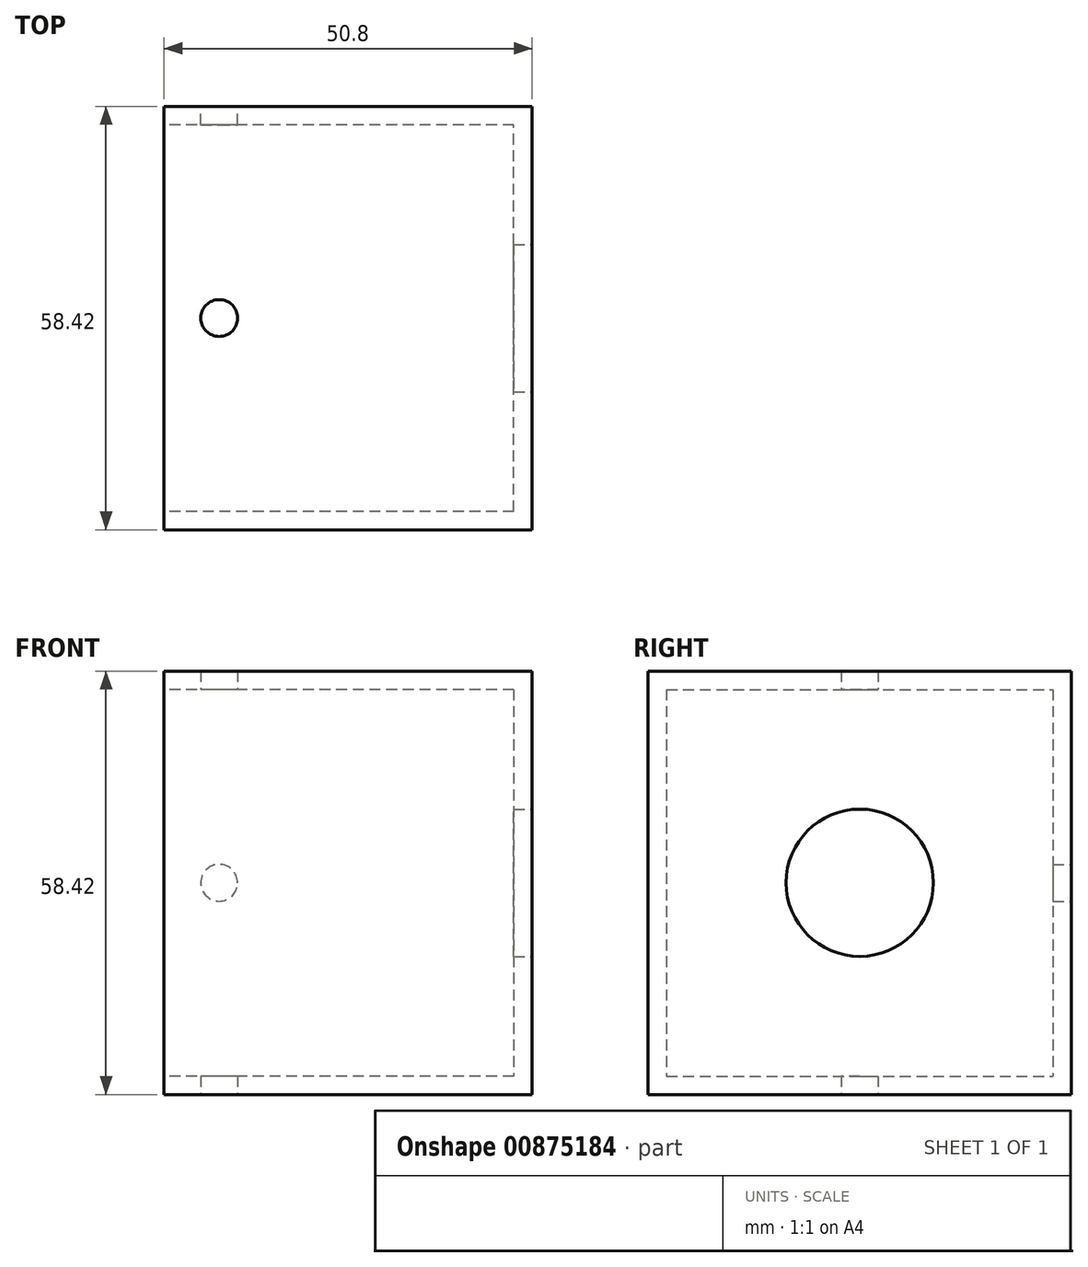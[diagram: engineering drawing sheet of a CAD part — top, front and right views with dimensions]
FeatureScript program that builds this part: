
annotation { "Feature Type Name" : "Feature", "Feature Type Description" : "" }
export const myFeature = defineFeature(function(context is Context, id is Id, definition is map)
    precondition{}
    {
        {
            var Q0;
            Q0=qCreatedBy(makeId("Right.planeOp"),FACE);
            var sketch = newSketch(context, id + "F0", { "sketchPlane" : qUnion([Q0])});
            skLineSegment(sketch, "E0.bottom", {"start": v(-29.2, 29.21) * mm, "end": v(29.21, 29.21) * mm});
            skLineSegment(sketch, "E0.top", {"start": v(-29.21, -29.2) * mm, "end": v(29.2, -29.2) * mm});
            skLineSegment(sketch, "E0.left", {"start": v(-29.2, 29.21) * mm, "end": v(-29.21, -29.2) * mm});
            skLineSegment(sketch, "E0.right", {"start": v(29.21, 29.21) * mm, "end": v(29.2, -29.2) * mm});
            skPoint(sketch, "E0.middle", {"position": v(0, 0) * mm});
            skSolve(sketch);
        }
        {
            var Q0;
            Q0=makeQuery(id+"F0.imprint","IMPRINT",FACE,{"disambiguationData":[TD([[makeQuery(id+"F0.imprint","IMPRINT",EDGE,{"derivedFrom":sQuery(id+"F0.wireOp",EDGE,"E0.bottom")}),-1.0]])]});
            extrude(context, id + "F1", {"entities" : qUnion([Q0]), "depth" : 50.8 * mm, "offsetDistance" : 25.4 * mm});
        }
        {
            var Q0;
            Q0=makeQuery(id+"F1.opExtrude","CAP_FACE",FACE,{"disambiguationData":[OSD([sQuery(id+"F0.wireOp",EDGE,"E0.bottom"),sQuery(id+"F0.wireOp",EDGE,"E0.top"),sQuery(id+"F0.wireOp",EDGE,"E0.left"),sQuery(id+"F0.wireOp",EDGE,"E0.right")])],"isStart":true});
            shell(context, id + "F2", {"entities" : qUnion([Q0]), "thickness" : 2.54 * mm});
        }
        {
            var Q0;
            Q0=makeQuery(id+"F1.opExtrude","CAP_FACE",FACE,{"disambiguationData":[OSD([sQuery(id+"F0.wireOp",EDGE,"E0.bottom"),sQuery(id+"F0.wireOp",EDGE,"E0.top"),sQuery(id+"F0.wireOp",EDGE,"E0.left"),sQuery(id+"F0.wireOp",EDGE,"E0.right")])],"isStart":false});
            var sketch = newSketch(context, id + "F3", { "sketchPlane" : qUnion([Q0])});
            skCircle(sketch, "E1", {"center": v(0, 0) * mm, "radius": 10.16 * mm});
            skSolve(sketch);
        }
        {
            var Q0;
            Q0=makeQuery(id+"F3.imprint","IMPRINT",FACE,{"disambiguationData":[TD([[makeQuery(id+"F3.imprint","IMPRINT",EDGE,{"derivedFrom":sQuery(id+"F3.wireOp",EDGE,"E1")}),1.0]])]});
            var Q1;
            Q1=sQuery(id+"F3.wireOp",EDGE,"E1");
            extrude(context, id + "F4", {"entities" : qUnion([Q0]), "operationType" : NewBodyOperationType.REMOVE, "surfaceEntities" : qUnion([Q1]), "oppositeDirection" : true, "depth" : 25.4 * mm, "offsetDistance" : 25.4 * mm});
        }
        {
            var Q0;
            Q0=makeQuery(id+"F1.opExtrude","SWEPT_FACE",FACE,{"disambiguationData":[OSD([sQuery(id+"F0.wireOp",EDGE,"E0.right")])]});
            var sketch = newSketch(context, id + "F5", { "sketchPlane" : qUnion([Q0])});
            skCircle(sketch, "E2", {"center": v(-7.62, 0) * mm, "radius": 2.54 * mm});
            skSolve(sketch);
        }
        {
            var Q0;
            Q0=makeQuery(id+"F5.imprint","IMPRINT",FACE,{"disambiguationData":[TD([[makeQuery(id+"F5.imprint","IMPRINT",EDGE,{"derivedFrom":sQuery(id+"F5.wireOp",EDGE,"E2")}),1.0]])]});
            var Q1;
            Q1=sQuery(id+"F5.wireOp",EDGE,"E2");
            extrude(context, id + "F6", {"entities" : qUnion([Q0]), "operationType" : NewBodyOperationType.REMOVE, "surfaceEntities" : qUnion([Q1]), "oppositeDirection" : true, "depth" : 39.12 * mm, "offsetDistance" : 25.4 * mm});
        }
        {
            var Q0;
            Q0=makeQuery(id+"F1.opExtrude","SWEPT_FACE",FACE,{"disambiguationData":[OSD([sQuery(id+"F0.wireOp",EDGE,"E0.top")])]});
            var sketch = newSketch(context, id + "F7", { "sketchPlane" : qUnion([Q0])});
            skCircle(sketch, "E3", {"center": v(7.62, 0) * mm, "radius": 2.54 * mm});
            skSolve(sketch);
        }
        {
            var Q0;
            Q0=makeQuery(id+"F7.imprint","IMPRINT",FACE,{"disambiguationData":[TD([[makeQuery(id+"F7.imprint","IMPRINT",EDGE,{"derivedFrom":sQuery(id+"F7.wireOp",EDGE,"E3")}),1.0]])]});
            var Q1;
            Q1=sQuery(id+"F7.wireOp",EDGE,"E3");
            extrude(context, id + "F8", {"entities" : qUnion([Q0]), "operationType" : NewBodyOperationType.REMOVE, "surfaceEntities" : qUnion([Q1]), "oppositeDirection" : true, "depth" : 80 * mm, "offsetDistance" : 25.4 * mm});
        }
    });
